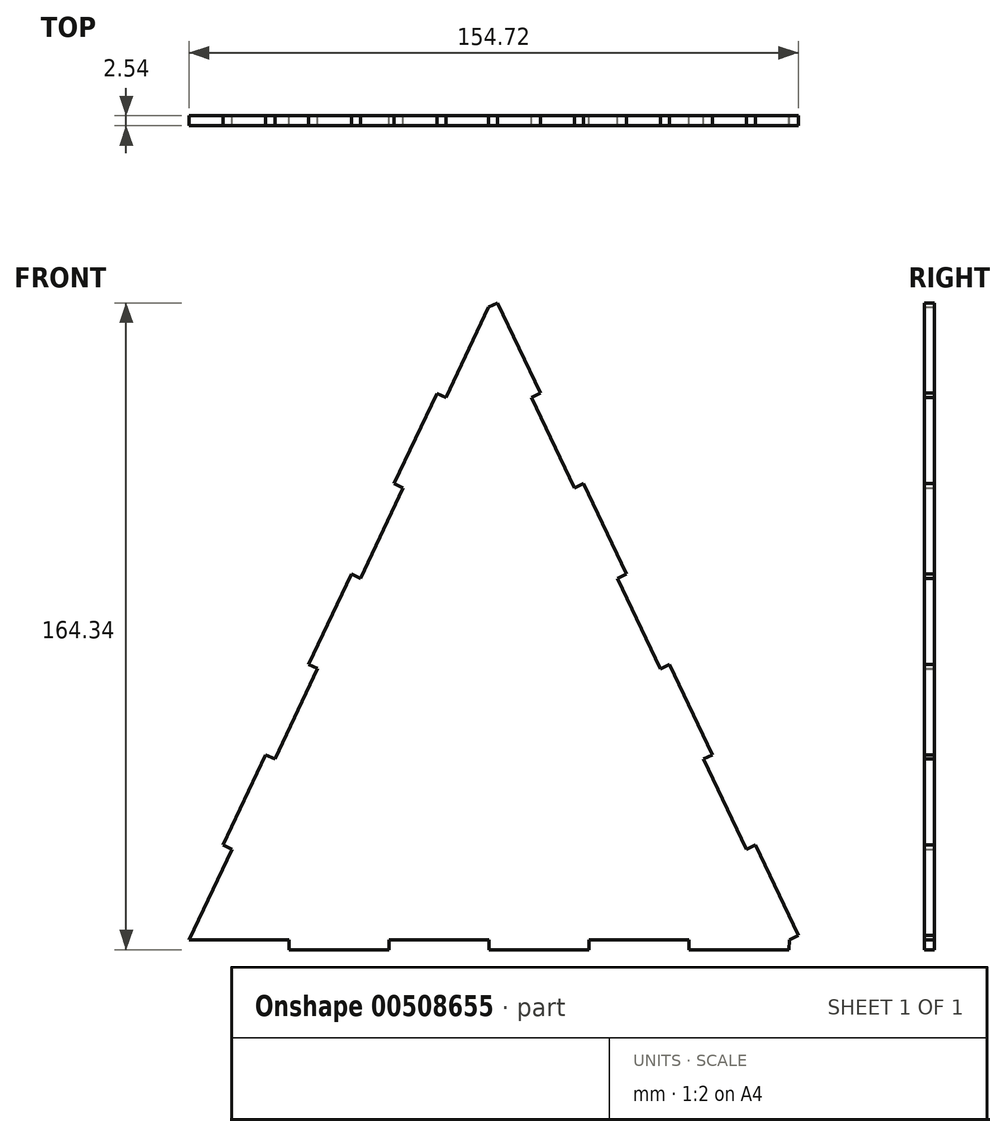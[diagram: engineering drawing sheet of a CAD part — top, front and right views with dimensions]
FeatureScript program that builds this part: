
annotation { "Feature Type Name" : "Feature", "Feature Type Description" : "" }
export const myFeature = defineFeature(function(context is Context, id is Id, definition is map)
    precondition{}
    {
        {
            var Q0;
            Q0=qCreatedBy(makeId("Front.planeOp"),FACE);
            var sketch = newSketch(context, id + "F0", { "sketchPlane" : qUnion([Q0])});
            skLineSegment(sketch, "E0", {"start": v(0, 85.84) * mm, "end": v(-76.07, -74.87) * mm});
            skLineSegment(sketch, "E1", {"start": v(-76.07, -74.87) * mm, "end": v(76.36, -74.87) * mm});
            skLineSegment(sketch, "E2", {"start": v(65.46, -51.93) * mm, "end": v(32.75, 16.9) * mm});
            skLineSegment(sketch, "E3", {"start": v(0, 85.84) * mm, "end": v(-10.87, 62.88) * mm});
            skLineSegment(sketch, "E4", {"start": v(-10.87, 62.88) * mm, "end": v(-13.16, 63.97) * mm});
            skLineSegment(sketch, "E5", {"start": v(-13.16, 63.97) * mm, "end": v(-24.03, 41) * mm});
            skLineSegment(sketch, "E6", {"start": v(-24.03, 41) * mm, "end": v(-21.73, 39.92) * mm});
            skLineSegment(sketch, "E7", {"start": v(-21.73, 39.92) * mm, "end": v(-32.6, 16.96) * mm});
            skLineSegment(sketch, "E8", {"start": v(-32.6, 16.96) * mm, "end": v(-34.9, 18.05) * mm});
            skLineSegment(sketch, "E9", {"start": v(-34.9, 18.05) * mm, "end": v(-45.76, -4.9) * mm});
            skLineSegment(sketch, "E10", {"start": v(-45.76, -4.9) * mm, "end": v(-43.47, -6) * mm});
            skLineSegment(sketch, "E11", {"start": v(-43.47, -6) * mm, "end": v(-54.33, -28.95) * mm});
            skLineSegment(sketch, "E12", {"start": v(-54.33, -28.95) * mm, "end": v(-56.63, -27.87) * mm});
            skLineSegment(sketch, "E13", {"start": v(-56.63, -27.87) * mm, "end": v(-67.5, -50.82) * mm});
            skLineSegment(sketch, "E14", {"start": v(-67.5, -50.82) * mm, "end": v(-65.2, -51.91) * mm});
            skLineSegment(sketch, "E15", {"start": v(-65.2, -51.91) * mm, "end": v(-76.07, -74.87) * mm});
            skLineSegment(sketch, "E16", {"start": v(21.8, 39.95) * mm, "end": v(32.75, 16.9) * mm});
            skLineSegment(sketch, "E17.trimOffspring", {"start": v(21.8, 39.95) * mm, "end": v(0, 85.84) * mm});
            skLineSegment(sketch, "E18", {"start": v(0, 85.84) * mm, "end": v(2.3, 86.93) * mm});
            skLineSegment(sketch, "E19", {"start": v(2.3, 86.93) * mm, "end": v(13.2, 63.99) * mm});
            skLineSegment(sketch, "E20", {"start": v(13.2, 63.99) * mm, "end": v(10.9, 62.9) * mm});
            skLineSegment(sketch, "E21", {"start": v(21.8, 39.95) * mm, "end": v(24.1, 41.04) * mm});
            skLineSegment(sketch, "E22", {"start": v(24.1, 41.04) * mm, "end": v(35, 18.1) * mm});
            skLineSegment(sketch, "E23", {"start": v(35, 18.1) * mm, "end": v(32.75, 16.9) * mm});
            skLineSegment(sketch, "E24", {"start": v(32.75, 16.9) * mm, "end": v(43.65, -6.04) * mm});
            skLineSegment(sketch, "E25", {"start": v(43.65, -6.04) * mm, "end": v(45.95, -4.95) * mm});
            skLineSegment(sketch, "E26", {"start": v(45.95, -4.95) * mm, "end": v(56.85, -27.9) * mm});
            skLineSegment(sketch, "E27", {"start": v(56.85, -27.9) * mm, "end": v(54.56, -28.98) * mm});
            skLineSegment(sketch, "E28", {"start": v(54.56, -28.98) * mm, "end": v(65.46, -51.93) * mm});
            skLineSegment(sketch, "E29", {"start": v(76.36, -74.87) * mm, "end": v(78.65, -73.78) * mm});
            skLineSegment(sketch, "E30", {"start": v(65.46, -51.93) * mm, "end": v(76.36, -74.87) * mm});
            skLineSegment(sketch, "E31", {"start": v(65.46, -51.93) * mm, "end": v(67.75, -50.84) * mm});
            skLineSegment(sketch, "E32", {"start": v(67.75, -50.84) * mm, "end": v(78.65, -73.78) * mm});
            skLineSegment(sketch, "E33", {"start": v(-76.07, -74.87) * mm, "end": v(-50.67, -74.87) * mm});
            skLineSegment(sketch, "E34", {"start": v(-50.67, -74.87) * mm, "end": v(-50.67, -77.4) * mm});
            skLineSegment(sketch, "E35", {"start": v(-50.67, -77.4) * mm, "end": v(-25.27, -77.4) * mm});
            skLineSegment(sketch, "E36", {"start": v(-25.27, -77.4) * mm, "end": v(-25.27, -74.87) * mm});
            skLineSegment(sketch, "E37", {"start": v(-25.27, -74.87) * mm, "end": v(0.13, -74.87) * mm});
            skLineSegment(sketch, "E38", {"start": v(0.13, -74.87) * mm, "end": v(0.13, -77.4) * mm});
            skLineSegment(sketch, "E39", {"start": v(0.13, -77.4) * mm, "end": v(25.53, -77.4) * mm});
            skLineSegment(sketch, "E40", {"start": v(25.53, -77.4) * mm, "end": v(25.53, -74.87) * mm});
            skLineSegment(sketch, "E41", {"start": v(25.53, -74.87) * mm, "end": v(50.93, -74.87) * mm});
            skLineSegment(sketch, "E42", {"start": v(50.93, -74.87) * mm, "end": v(50.93, -77.4) * mm});
            skLineSegment(sketch, "E43", {"start": v(50.93, -77.4) * mm, "end": v(76.33, -77.4) * mm});
            skLineSegment(sketch, "E44", {"start": v(76.33, -77.4) * mm, "end": v(76.36, -74.87) * mm});
            skSolve(sketch);
        }
        {
            var Q0;
            Q0 = qSketchRegion(id + "F0", true);
            extrude(context, id + "F1", {"entities" : qUnion([Q0]), "depth" : 2.54 * mm, "offsetDistance" : 25.4 * mm});
        }
    });
